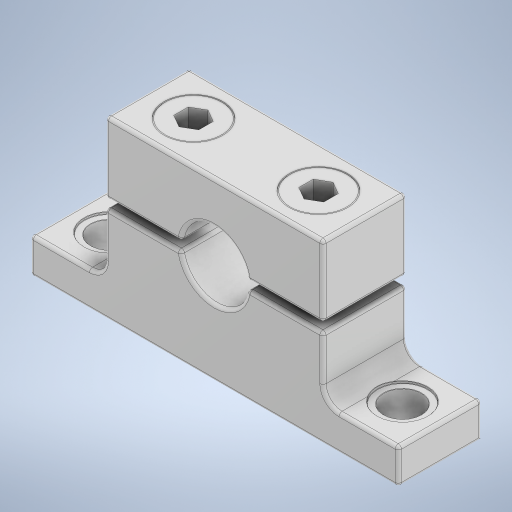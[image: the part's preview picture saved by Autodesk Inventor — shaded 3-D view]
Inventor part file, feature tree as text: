
AUTODESK INVENTOR PART (.ipt)
format: ipt  version: 2023 (Build 270158000, 158)  size: 429,568 bytes
history: mixed  units: in
note: dims shown in document units (in); Inventor stores cm internally (conversion verified against a paired STEP export)
features: fillet x2, other x1, mirror x1, imported_body x1
ambient origin geometry x8: Origin, YZ Plane, XZ Plane, XY Plane, X Axis, Y Axis, Z Axis, Center Point
bodies: Solid1 (imported_parasolid), Solid2 (imported_parasolid), Solid3 (imported_parasolid), Solid4 (imported_parasolid)
feature tree (5):
  other  "Cut-Extrude6"
  mirror  "Mirror1"
  fillet  "Fillet1"  [1 undecoded]
  fillet  "Fillet3"  [1 undecoded]
  imported_body  NMx_Import_Brep_tag  [imported B-rep: ~91 faces, bbox_mm=[32.75, 21.0, 10.0]]
note: 2 required parameter values undecoded (feature->parameter linkage not recoverable at this tier; creation-order binding heuristic only, values carry confidence <= 0.55)
